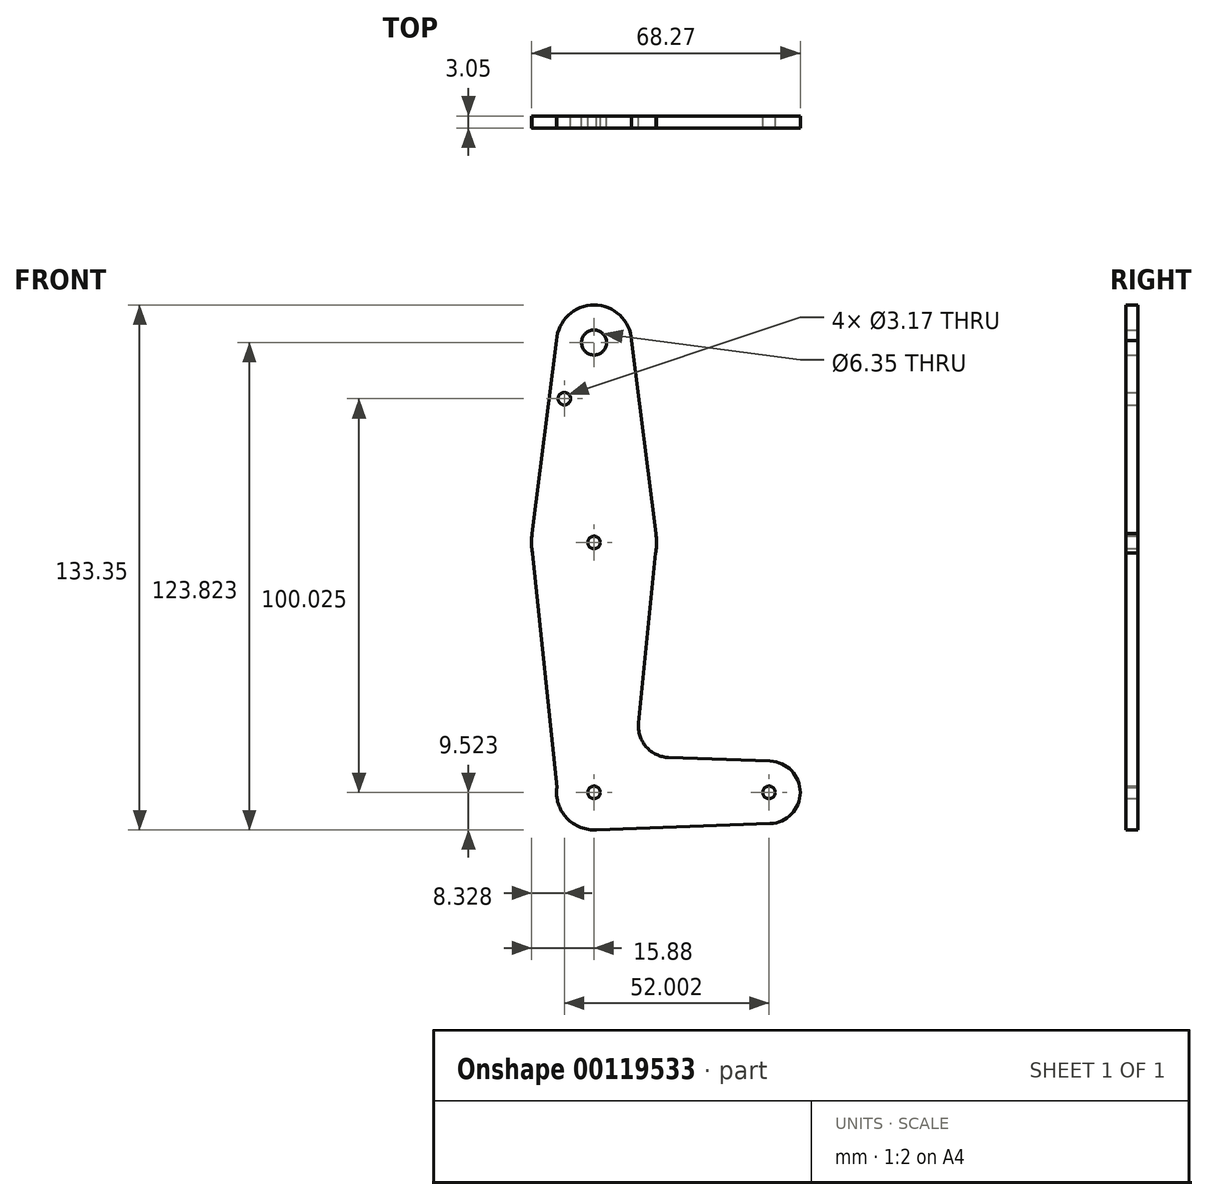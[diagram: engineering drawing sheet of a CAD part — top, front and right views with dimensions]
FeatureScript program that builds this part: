
annotation { "Feature Type Name" : "Feature", "Feature Type Description" : "" }
export const myFeature = defineFeature(function(context is Context, id is Id, definition is map)
    precondition{}
    {
        {
            var Q0;
            Q0=qCreatedBy(makeId("Front.planeOp"),FACE);
            var sketch = newSketch(context, id + "F0", { "sketchPlane" : qUnion([Q0])});
            skCircle(sketch, "E0", {"center": v(0, 83.48) * mm, "radius": 9.53 * mm});
            skCircle(sketch, "E1", {"center": v(0, 32.68) * mm, "radius": 15.88 * mm});
            skCircle(sketch, "E2", {"center": v(0, -30.82) * mm, "radius": 9.53 * mm});
            skCircle(sketch, "E3", {"center": v(44.45, -30.82) * mm, "radius": 7.94 * mm});
            skLineSegment(sketch, "E4", {"start": v(9.5, 84.02) * mm, "end": v(15.72, 34.91) * mm});
            skLineSegment(sketch, "E5", {"start": v(18.96, -21.97) * mm, "end": v(44.73, -22.88) * mm});
            skLineSegment(sketch, "E6", {"start": v(0, -40.34) * mm, "end": v(44.73, -38.75) * mm});
            skLineSegment(sketch, "E7", {"start": v(-9.44, -29.52) * mm, "end": v(-15.87, 32.24) * mm});
            skLineSegment(sketch, "E8", {"start": v(-15.72, 34.91) * mm, "end": v(-9.5, 84.02) * mm});
            skPoint(sketch, "E9.newPointB", {"position": v(0, -21.3) * mm});
            skCircle(sketch, "E10", {"center": v(0, 32.68) * mm, "radius": 1.59 * mm});
            skCircle(sketch, "E11", {"center": v(0, -30.82) * mm, "radius": 1.59 * mm});
            skCircle(sketch, "E12", {"center": v(44.45, -30.82) * mm, "radius": 1.59 * mm});
            skCircle(sketch, "E13", {"center": v(0, 83.48) * mm, "radius": 3.18 * mm});
            skCircle(sketch, "E14", {"center": v(-7.55, 69.2) * mm, "radius": 1.59 * mm});
            skLineSegment(sketch, "E15", {"start": v(15.87, 32.24) * mm, "end": v(11.33, -13.23) * mm});
            skArc(sketch, "E16.filletArc", {"start": v(11.33, -13.23) * mm, "mid": v(13.25, -19.25) * mm, "end": v(18.96, -21.97) * mm});
            skSolve(sketch);
        }
        {
            var Q0;
            Q0 = qSketchRegion(id + "F0", true);
            extrude(context, id + "F1", {"entities" : qUnion([Q0]), "depth" : 3.05 * mm});
        }
    });
